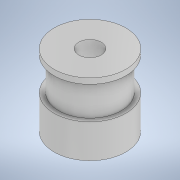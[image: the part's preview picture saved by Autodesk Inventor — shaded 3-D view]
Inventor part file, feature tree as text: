
AUTODESK INVENTOR PART (.ipt)
format: ipt  version: 2021 (Build 250183000, 183)  size: 116,224 bytes
history: native  units: mm
features: extrude x2, sketch x2, plane x1
ambient origin geometry x8: Origin, YZ Plane, XZ Plane, XY Plane, X Axis, Y Axis, Z Axis, Center Point
bodies: Solid1 (feature_tree)
feature tree (5):
  extrude  "Extrusion1"  Depth=16.0mm
  plane  "Work Plane1"
  extrude  "Extrusion2"  [1 undecoded]
  sketch  "Sketch1"  dims[d0=16.0mm d1=5.0mm]
  sketch  "Sketch2"  dims[d2=16.0mm d3=0.0mm d4=-1.25mm d5=1.0mm d6=7.25mm d7=0.0mm]
note: 1 required parameter value undecoded (feature->parameter linkage not recoverable at this tier; creation-order binding heuristic only, values carry confidence <= 0.55)
